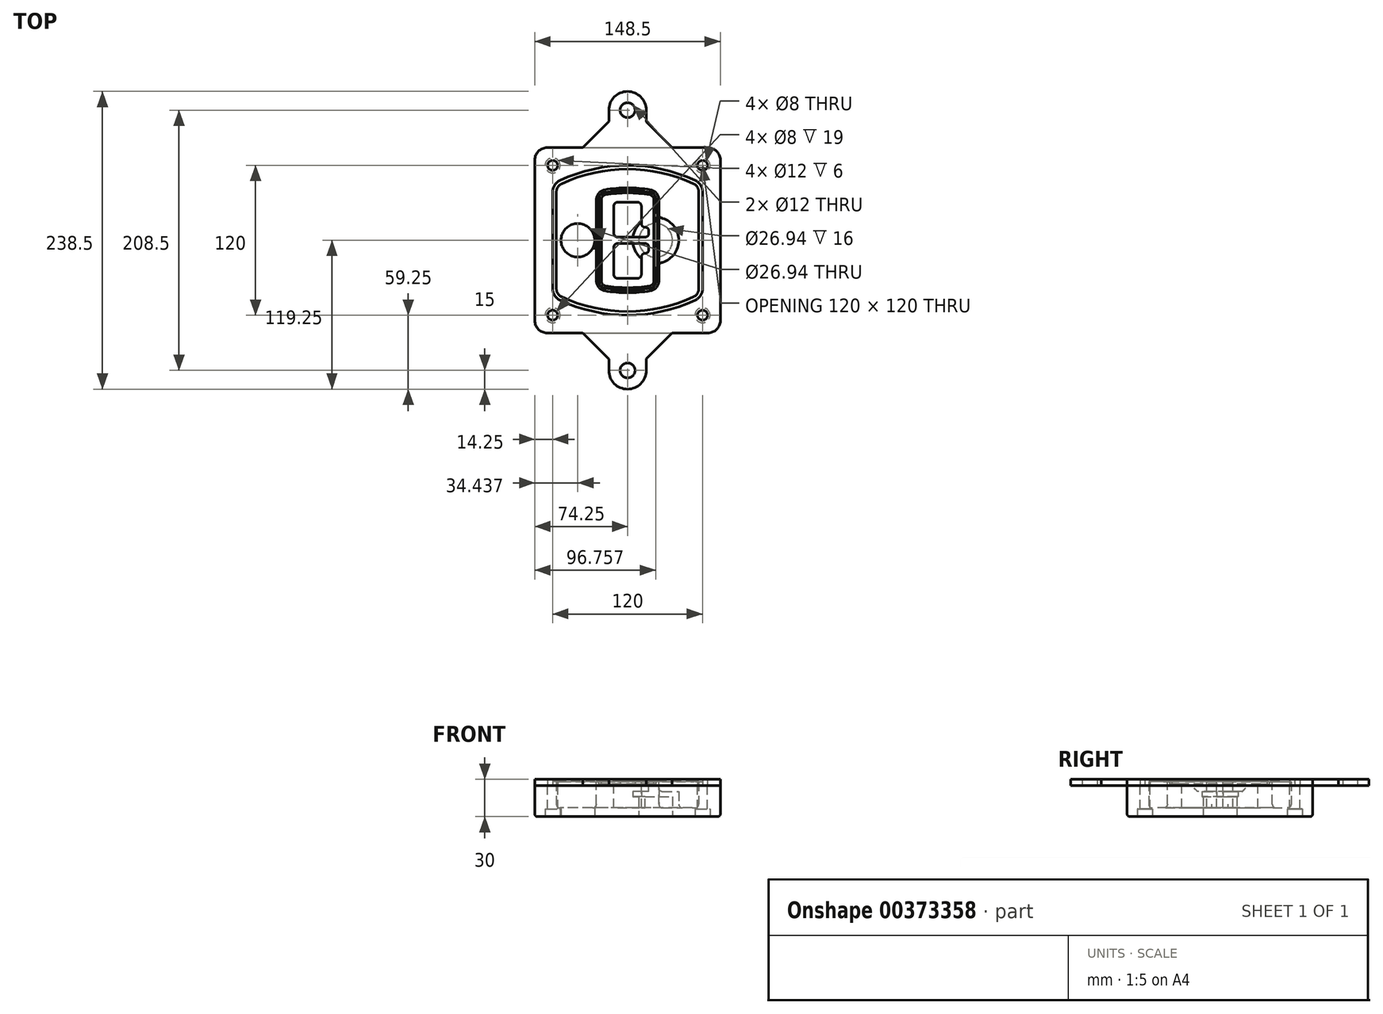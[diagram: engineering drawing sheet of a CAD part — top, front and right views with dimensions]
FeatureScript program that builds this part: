
annotation { "Feature Type Name" : "Feature", "Feature Type Description" : "" }
export const myFeature = defineFeature(function(context is Context, id is Id, definition is map)
    precondition{}
    {
        {
            var Q0;
            Q0=qCreatedBy(makeId("Top.planeOp"),FACE);
            var sketch = newSketch(context, id + "F0", { "sketchPlane" : qUnion([Q0])});
            skPoint(sketch, "E0.rect.middle", {"position": v(0, 0) * mm});
            skLineSegment(sketch, "E1.bottom", {"start": v(-64.25, -74.25) * mm, "end": v(64.25, -74.25) * mm});
            skLineSegment(sketch, "E1.top", {"start": v(-64.25, 74.25) * mm, "end": v(64.25, 74.25) * mm});
            skLineSegment(sketch, "E1.left", {"start": v(-74.25, -64.25) * mm, "end": v(-74.25, 64.25) * mm});
            skLineSegment(sketch, "E1.right", {"start": v(74.25, -64.25) * mm, "end": v(74.25, 64.25) * mm});
            skLineSegment(sketch, "E2", {"start": v(-74.25, 74.25) * mm, "end": v(74.25, -74.25) * mm, "construction": true});
            skLineSegment(sketch, "E3", {"start": v(74.25, 74.25) * mm, "end": v(-74.25, -74.25) * mm, "construction": true});
            skCircle(sketch, "E4", {"center": v(-60, 60) * mm, "radius": 4 * mm});
            skCircle(sketch, "E5", {"center": v(60, 60) * mm, "radius": 4 * mm});
            skCircle(sketch, "E6", {"center": v(60, -60) * mm, "radius": 4 * mm});
            skCircle(sketch, "E7", {"center": v(-60, -60) * mm, "radius": 4 * mm});
            skLineSegment(sketch, "E8", {"start": v(-60, 60) * mm, "end": v(60, 60) * mm, "construction": true});
            skLineSegment(sketch, "E9", {"start": v(60, 60) * mm, "end": v(60, -60) * mm, "construction": true});
            skLineSegment(sketch, "E10", {"start": v(60, -60) * mm, "end": v(-60, -60) * mm, "construction": true});
            skLineSegment(sketch, "E11", {"start": v(-60, -60) * mm, "end": v(-60, 60) * mm, "construction": true});
            skLineSegment(sketch, "E12", {"start": v(-60, 38.83) * mm, "end": v(-60, -38.83) * mm});
            skLineSegment(sketch, "E13", {"start": v(60, 38.83) * mm, "end": v(60, -38.83) * mm});
            skArc(sketch, "E14", {"start": v(54.26, 47.88) * mm, "mid": v(0, 60) * mm, "end": v(-54.26, 47.88) * mm});
            skArc(sketch, "E15", {"start": v(-54.26, -47.88) * mm, "mid": v(0, -60) * mm, "end": v(54.26, -47.88) * mm});
            skLineSegment(sketch, "E16", {"start": v(-60, 0) * mm, "end": v(60, 0) * mm, "construction": true});
            skPoint(sketch, "E17.visualSharp", {"position": v(-60, -45) * mm});
            skArc(sketch, "E17.filletArc", {"start": v(-60, -38.83) * mm, "mid": v(-58.44, -44.2) * mm, "end": v(-54.26, -47.88) * mm});
            skPoint(sketch, "E18.visualSharp", {"position": v(-60, 45) * mm});
            skArc(sketch, "E18.filletArc", {"start": v(-54.26, 47.88) * mm, "mid": v(-58.44, 44.2) * mm, "end": v(-60, 38.83) * mm});
            skPoint(sketch, "E19.visualSharp", {"position": v(60, 45) * mm});
            skArc(sketch, "E19.filletArc", {"start": v(60, 38.83) * mm, "mid": v(58.44, 44.2) * mm, "end": v(54.26, 47.88) * mm});
            skPoint(sketch, "E20.visualSharp", {"position": v(60, -45) * mm});
            skArc(sketch, "E20.filletArc", {"start": v(54.26, -47.88) * mm, "mid": v(58.44, -44.2) * mm, "end": v(60, -38.83) * mm});
            skPoint(sketch, "E21.visualSharp", {"position": v(-74.25, 74.25) * mm});
            skArc(sketch, "E21.filletArc", {"start": v(-64.25, 74.25) * mm, "mid": v(-71.32, 71.32) * mm, "end": v(-74.25, 64.25) * mm});
            skPoint(sketch, "E22.visualSharp", {"position": v(74.25, 74.25) * mm});
            skArc(sketch, "E22.filletArc", {"start": v(74.25, 64.25) * mm, "mid": v(71.32, 71.32) * mm, "end": v(64.25, 74.25) * mm});
            skPoint(sketch, "E23.visualSharp", {"position": v(74.25, -74.25) * mm});
            skArc(sketch, "E23.filletArc", {"start": v(64.25, -74.25) * mm, "mid": v(71.32, -71.32) * mm, "end": v(74.25, -64.25) * mm});
            skPoint(sketch, "E24.visualSharp", {"position": v(-74.25, -74.25) * mm});
            skArc(sketch, "E24.filletArc", {"start": v(-74.25, -64.25) * mm, "mid": v(-71.32, -71.32) * mm, "end": v(-64.25, -74.25) * mm});
            skArc(sketch, "E25.0", {"start": v(57, 38.83) * mm, "mid": v(55.9, 42.58) * mm, "end": v(52.98, 45.17) * mm});
            skLineSegment(sketch, "E25.1", {"start": v(57, 38.83) * mm, "end": v(57, -38.83) * mm});
            skArc(sketch, "E25.2", {"start": v(52.98, -45.17) * mm, "mid": v(55.9, -42.58) * mm, "end": v(57, -38.83) * mm});
            skArc(sketch, "E25.3", {"start": v(-52.98, -45.17) * mm, "mid": v(0, -57) * mm, "end": v(52.98, -45.17) * mm});
            skArc(sketch, "E25.4", {"start": v(-57, -38.83) * mm, "mid": v(-55.9, -42.58) * mm, "end": v(-52.98, -45.17) * mm});
            skArc(sketch, "E25.5", {"start": v(52.98, 45.17) * mm, "mid": v(0, 57) * mm, "end": v(-52.98, 45.17) * mm});
            skLineSegment(sketch, "E25.6", {"start": v(-57, 38.83) * mm, "end": v(-57, -38.83) * mm});
            skArc(sketch, "E25.7", {"start": v(-52.98, 45.17) * mm, "mid": v(-55.9, 42.58) * mm, "end": v(-57, 38.83) * mm});
            skArc(sketch, "E26.0", {"start": v(-55.96, 51.5) * mm, "mid": v(-61.82, 46.33) * mm, "end": v(-64, 38.83) * mm});
            skArc(sketch, "E26.1", {"start": v(55.96, 51.5) * mm, "mid": v(0, 64) * mm, "end": v(-55.96, 51.5) * mm});
            skArc(sketch, "E26.2", {"start": v(64, 38.83) * mm, "mid": v(61.82, 46.33) * mm, "end": v(55.96, 51.5) * mm});
            skLineSegment(sketch, "E26.3", {"start": v(64, 38.83) * mm, "end": v(64, -38.83) * mm});
            skArc(sketch, "E26.4", {"start": v(55.96, -51.5) * mm, "mid": v(61.82, -46.33) * mm, "end": v(64, -38.83) * mm});
            skLineSegment(sketch, "E26.5", {"start": v(-64, 38.83) * mm, "end": v(-64, -38.83) * mm});
            skArc(sketch, "E26.6", {"start": v(-55.96, -51.5) * mm, "mid": v(0, -64) * mm, "end": v(55.96, -51.5) * mm});
            skArc(sketch, "E26.7", {"start": v(-64, -38.83) * mm, "mid": v(-61.82, -46.33) * mm, "end": v(-55.96, -51.5) * mm});
            skSolve(sketch);
        }
        {
            var Q0;
            Q0=makeQuery(id+"F0.imprint","IMPRINT",FACE,{"disambiguationData":[TD([[makeQuery(id+"F0.imprint","IMPRINT",EDGE,{"derivedFrom":sQuery(id+"F0.wireOp",EDGE,"E1.bottom")}),1.0]])]});
            var Q1;
            Q1=makeQuery(id+"F0.imprint","IMPRINT",FACE,{"disambiguationData":[TD([[makeQuery(id+"F0.imprint","IMPRINT",EDGE,{"derivedFrom":sQuery(id+"F0.wireOp",EDGE,"E12")}),1.0]])]});
            var Q2;
            Q2=makeQuery(id+"F0.imprint","IMPRINT",FACE,{"disambiguationData":[TD([[makeQuery(id+"F0.imprint","IMPRINT",EDGE,{"derivedFrom":sQuery(id+"F0.wireOp",EDGE,"E25.0")}),1.0]])]});
            var Q3;
            Q3=makeQuery(id+"F0.imprint","IMPRINT",FACE,{"disambiguationData":[TD([[makeQuery(id+"F0.imprint","IMPRINT",EDGE,{"derivedFrom":sQuery(id+"F0.wireOp",EDGE,"E12")}),-1.0]])]});
            extrude(context, id + "F1", {"entities" : qUnion([Q0, Q1, Q2, Q3]), "oppositeDirection" : true, "depth" : 25 * mm});
        }
        {
            var Q0;
            Q0=makeQuery(id+"F0.imprint","IMPRINT",FACE,{"disambiguationData":[TD([[makeQuery(id+"F0.imprint","IMPRINT",EDGE,{"derivedFrom":sQuery(id+"F0.wireOp",EDGE,"E12")}),1.0]])]});
            extrude(context, id + "F2", {"entities" : qUnion([Q0]), "operationType" : NewBodyOperationType.ADD, "depth" : 3 * mm});
        }
        {
            var Q0;
            Q0=makeQuery(id+"F0.imprint","IMPRINT",FACE,{"disambiguationData":[TD([[makeQuery(id+"F0.imprint","IMPRINT",EDGE,{"derivedFrom":sQuery(id+"F0.wireOp",EDGE,"E25.0")}),1.0]])]});
            extrude(context, id + "F3", {"entities" : qUnion([Q0]), "operationType" : NewBodyOperationType.REMOVE, "oppositeDirection" : true, "depth" : 18 * mm});
        }
        {
            var Q0;
            Q0=makeQuery(id+"F2.opExtrude","CAP_FACE",FACE,{"disambiguationData":[OSD([sQuery(id+"F0.wireOp",EDGE,"E12"),sQuery(id+"F0.wireOp",EDGE,"E13"),sQuery(id+"F0.wireOp",EDGE,"E14"),sQuery(id+"F0.wireOp",EDGE,"E15"),sQuery(id+"F0.wireOp",EDGE,"E17.filletArc"),sQuery(id+"F0.wireOp",EDGE,"E18.filletArc"),sQuery(id+"F0.wireOp",EDGE,"E19.filletArc"),sQuery(id+"F0.wireOp",EDGE,"E20.filletArc"),sQuery(id+"F0.wireOp",EDGE,"E25.0"),sQuery(id+"F0.wireOp",EDGE,"E25.1"),sQuery(id+"F0.wireOp",EDGE,"E25.2"),sQuery(id+"F0.wireOp",EDGE,"E25.3"),sQuery(id+"F0.wireOp",EDGE,"E25.4"),sQuery(id+"F0.wireOp",EDGE,"E25.5"),sQuery(id+"F0.wireOp",EDGE,"E25.6"),sQuery(id+"F0.wireOp",EDGE,"E25.7")])],"isStart":false});
            var sketch = newSketch(context, id + "F4", { "sketchPlane" : qUnion([Q0])});
            skArc(sketch, "E27.0", {"start": v(-18.34, -40.45) * mm, "mid": v(0, -42) * mm, "end": v(18.34, -40.45) * mm});
            skArc(sketch, "E28.0", {"start": v(18.34, 40.45) * mm, "mid": v(0, 42) * mm, "end": v(-18.34, 40.45) * mm});
            skLineSegment(sketch, "E29", {"start": v(-25, 32.57) * mm, "end": v(-25, -32.57) * mm});
            skLineSegment(sketch, "E30", {"start": v(25, 32.57) * mm, "end": v(25, -32.57) * mm});
            skLineSegment(sketch, "E31", {"start": v(-25, 39.1) * mm, "end": v(25, 39.1) * mm, "construction": true});
            skLineSegment(sketch, "E32", {"start": v(-25, -39.1) * mm, "end": v(25, -39.1) * mm, "construction": true});
            skPoint(sketch, "E33.visualSharp", {"position": v(-25, 39.1) * mm});
            skArc(sketch, "E33.filletArc", {"start": v(-18.34, 40.45) * mm, "mid": v(-23.11, 37.73) * mm, "end": v(-25, 32.57) * mm});
            skPoint(sketch, "E34.visualSharp", {"position": v(25, 39.1) * mm});
            skArc(sketch, "E34.filletArc", {"start": v(25, 32.57) * mm, "mid": v(23.11, 37.73) * mm, "end": v(18.34, 40.45) * mm});
            skPoint(sketch, "E35.visualSharp", {"position": v(25, -39.1) * mm});
            skArc(sketch, "E35.filletArc", {"start": v(18.34, -40.45) * mm, "mid": v(23.11, -37.73) * mm, "end": v(25, -32.57) * mm});
            skPoint(sketch, "E36.visualSharp", {"position": v(-25, -39.1) * mm});
            skArc(sketch, "E36.filletArc", {"start": v(-25, -32.57) * mm, "mid": v(-23.11, -37.73) * mm, "end": v(-18.34, -40.45) * mm});
            skArc(sketch, "E37.0", {"start": v(52.98, 45.17) * mm, "mid": v(0, 57) * mm, "end": v(-52.98, 45.17) * mm});
            skArc(sketch, "E37.1", {"start": v(-52.98, 45.17) * mm, "mid": v(-55.9, 42.58) * mm, "end": v(-57, 38.83) * mm});
            skLineSegment(sketch, "E37.2", {"start": v(-57, 38.83) * mm, "end": v(-57, -38.83) * mm});
            skArc(sketch, "E37.3", {"start": v(-57, -38.83) * mm, "mid": v(-55.9, -42.58) * mm, "end": v(-52.98, -45.17) * mm});
            skArc(sketch, "E37.4", {"start": v(-52.98, -45.17) * mm, "mid": v(0, -57) * mm, "end": v(52.98, -45.17) * mm});
            skArc(sketch, "E37.5", {"start": v(52.98, -45.17) * mm, "mid": v(55.9, -42.58) * mm, "end": v(57, -38.83) * mm});
            skLineSegment(sketch, "E37.6", {"start": v(57, 38.83) * mm, "end": v(57, -38.83) * mm});
            skArc(sketch, "E37.7", {"start": v(57, 38.83) * mm, "mid": v(55.9, 42.58) * mm, "end": v(52.98, 45.17) * mm});
            skLineSegment(sketch, "E38.0", {"start": v(23, 32.57) * mm, "end": v(23, -32.57) * mm});
            skArc(sketch, "E38.1", {"start": v(18, -38.48) * mm, "mid": v(21.58, -36.44) * mm, "end": v(23, -32.57) * mm});
            skArc(sketch, "E38.2", {"start": v(-18, -38.48) * mm, "mid": v(0, -40) * mm, "end": v(18, -38.48) * mm});
            skArc(sketch, "E38.3", {"start": v(-23, -32.57) * mm, "mid": v(-21.58, -36.44) * mm, "end": v(-18, -38.48) * mm});
            skLineSegment(sketch, "E38.4", {"start": v(-23, 32.57) * mm, "end": v(-23, -32.57) * mm});
            skArc(sketch, "E38.5", {"start": v(23, 32.57) * mm, "mid": v(21.58, 36.44) * mm, "end": v(18, 38.48) * mm});
            skArc(sketch, "E38.6", {"start": v(-18, 38.48) * mm, "mid": v(-21.58, 36.44) * mm, "end": v(-23, 32.57) * mm});
            skArc(sketch, "E38.7", {"start": v(18, 38.48) * mm, "mid": v(0, 40) * mm, "end": v(-18, 38.48) * mm});
            skArc(sketch, "E39.0", {"start": v(21, 32.57) * mm, "mid": v(20.06, 35.15) * mm, "end": v(17.67, 36.5) * mm});
            skLineSegment(sketch, "E39.1", {"start": v(21, 32.57) * mm, "end": v(21, -32.57) * mm});
            skArc(sketch, "E39.2", {"start": v(17.67, -36.5) * mm, "mid": v(20.06, -35.15) * mm, "end": v(21, -32.57) * mm});
            skArc(sketch, "E39.3", {"start": v(-17.67, -36.5) * mm, "mid": v(0, -38) * mm, "end": v(17.67, -36.5) * mm});
            skArc(sketch, "E39.4", {"start": v(-21, -32.57) * mm, "mid": v(-20.06, -35.15) * mm, "end": v(-17.67, -36.5) * mm});
            skArc(sketch, "E39.5", {"start": v(17.67, 36.5) * mm, "mid": v(0, 38) * mm, "end": v(-17.67, 36.5) * mm});
            skLineSegment(sketch, "E39.6", {"start": v(-21, 32.57) * mm, "end": v(-21, -32.57) * mm});
            skArc(sketch, "E39.7", {"start": v(-17.67, 36.5) * mm, "mid": v(-20.06, 35.15) * mm, "end": v(-21, 32.57) * mm});
            skLineSegment(sketch, "E40", {"start": v(-25, 0) * mm, "end": v(25, 0) * mm, "construction": true});
            skLineSegment(sketch, "E41", {"start": v(-11, 5.5) * mm, "end": v(-11, 27.5) * mm});
            skLineSegment(sketch, "E42", {"start": v(-8, 30.5) * mm, "end": v(8, 30.5) * mm});
            skLineSegment(sketch, "E43", {"start": v(11, 27.5) * mm, "end": v(11, 13.5) * mm});
            skLineSegment(sketch, "E44", {"start": v(14, 10.5) * mm, "end": v(14, 10.5) * mm});
            skLineSegment(sketch, "E45", {"start": v(17, 7.5) * mm, "end": v(17, 5.5) * mm});
            skLineSegment(sketch, "E46", {"start": v(14, 2.5) * mm, "end": v(-8, 2.5) * mm});
            skPoint(sketch, "E47.visualSharp", {"position": v(-11, 30.5) * mm});
            skArc(sketch, "E47.filletArc", {"start": v(-8, 30.5) * mm, "mid": v(-10.12, 29.62) * mm, "end": v(-11, 27.5) * mm});
            skPoint(sketch, "E48.visualSharp", {"position": v(11, 30.5) * mm});
            skArc(sketch, "E48.filletArc", {"start": v(11, 27.5) * mm, "mid": v(10.12, 29.62) * mm, "end": v(8, 30.5) * mm});
            skPoint(sketch, "E49.visualSharp", {"position": v(11, 10.5) * mm});
            skArc(sketch, "E49.filletArc", {"start": v(11, 13.5) * mm, "mid": v(11.88, 11.38) * mm, "end": v(14, 10.5) * mm});
            skPoint(sketch, "E50.visualSharp", {"position": v(17, 10.5) * mm});
            skArc(sketch, "E50.filletArc", {"start": v(17, 7.5) * mm, "mid": v(16.12, 9.62) * mm, "end": v(14, 10.5) * mm});
            skPoint(sketch, "E51.visualSharp", {"position": v(17, 2.5) * mm});
            skArc(sketch, "E51.filletArc", {"start": v(14, 2.5) * mm, "mid": v(16.12, 3.38) * mm, "end": v(17, 5.5) * mm});
            skPoint(sketch, "E52.visualSharp", {"position": v(-11, 2.5) * mm});
            skArc(sketch, "E52.filletArc", {"start": v(-11, 5.5) * mm, "mid": v(-10.12, 3.38) * mm, "end": v(-8, 2.5) * mm});
            skLineSegment(sketch, "E53.0.MirrorCS", {"start": v(14, -2.5) * mm, "end": v(-8, -2.5) * mm});
            skArc(sketch, "E54.0.MirrorCS", {"start": v(-11, -5.5) * mm, "mid": v(-10.12, -3.38) * mm, "end": v(-8, -2.5) * mm});
            skLineSegment(sketch, "E55.0.MirrorCS", {"start": v(-11, -5.5) * mm, "end": v(-11, -27.5) * mm});
            skArc(sketch, "E56.0.MirrorCS", {"start": v(-8, -30.5) * mm, "mid": v(-10.12, -29.62) * mm, "end": v(-11, -27.5) * mm});
            skLineSegment(sketch, "E57.0.MirrorCS", {"start": v(-8, -30.5) * mm, "end": v(8, -30.5) * mm});
            skArc(sketch, "E58.0.MirrorCS", {"start": v(11, -27.5) * mm, "mid": v(10.12, -29.62) * mm, "end": v(8, -30.5) * mm});
            skLineSegment(sketch, "E59.0.MirrorCS", {"start": v(11, -27.5) * mm, "end": v(11, -13.5) * mm});
            skArc(sketch, "E60.0.MirrorCS", {"start": v(11, -13.5) * mm, "mid": v(11.88, -11.38) * mm, "end": v(14, -10.5) * mm});
            skArc(sketch, "E61.0.MirrorCS", {"start": v(17, -7.5) * mm, "mid": v(16.12, -9.62) * mm, "end": v(14, -10.5) * mm});
            skLineSegment(sketch, "E62.0.MirrorCS", {"start": v(17, -7.5) * mm, "end": v(17, -5.5) * mm});
            skArc(sketch, "E63.0.MirrorCS", {"start": v(14, -2.5) * mm, "mid": v(16.12, -3.38) * mm, "end": v(17, -5.5) * mm});
            skSolve(sketch);
        }
        {
            var Q0;
            Q0=makeQuery(id+"F4.imprint","IMPRINT",FACE,{"disambiguationData":[TD([[makeQuery(id+"F4.imprint","IMPRINT",EDGE,{"derivedFrom":sQuery(id+"F4.wireOp",EDGE,"E27.0")}),1.0]])]});
            var Q1;
            Q1=makeQuery(id+"F4.imprint","IMPRINT",FACE,{"disambiguationData":[TD([[makeQuery(id+"F4.imprint","IMPRINT",EDGE,{"derivedFrom":sQuery(id+"F4.wireOp",EDGE,"E38.0")}),-1.0]])]});
            var Q2;
            Q2=makeQuery(id+"F4.imprint","IMPRINT",FACE,{"disambiguationData":[TD([[makeQuery(id+"F4.imprint","IMPRINT",EDGE,{"derivedFrom":sQuery(id+"F4.wireOp",EDGE,"E39.0")}),1.0]])]});
            extrude(context, id + "F5", {"entities" : qUnion([Q0, Q1, Q2]), "operationType" : NewBodyOperationType.ADD, "endBound" : BoundingType.UP_TO_NEXT, "oppositeDirection" : true, "depth" : 25 * mm});
        }
        {
            var Q0;
            Q0=makeQuery(id+"F4.imprint","IMPRINT",FACE,{"disambiguationData":[TD([[makeQuery(id+"F4.imprint","IMPRINT",EDGE,{"derivedFrom":sQuery(id+"F4.wireOp",EDGE,"E38.0")}),-1.0]])]});
            extrude(context, id + "F6", {"entities" : qUnion([Q0]), "operationType" : NewBodyOperationType.REMOVE, "oppositeDirection" : true, "depth" : 2 * mm});
        }
        {
            var Q0;
            Q0=makeQuery(id+"F1.opExtrude","CAP_FACE",FACE,{"disambiguationData":[OSD([sQuery(id+"F0.wireOp",EDGE,"E1.bottom"),sQuery(id+"F0.wireOp",EDGE,"E1.top"),sQuery(id+"F0.wireOp",EDGE,"E1.left"),sQuery(id+"F0.wireOp",EDGE,"E1.right"),sQuery(id+"F0.wireOp",EDGE,"E4"),sQuery(id+"F0.wireOp",EDGE,"E5"),sQuery(id+"F0.wireOp",EDGE,"E6"),sQuery(id+"F0.wireOp",EDGE,"E7"),sQuery(id+"F0.wireOp",EDGE,"E21.filletArc"),sQuery(id+"F0.wireOp",EDGE,"E22.filletArc"),sQuery(id+"F0.wireOp",EDGE,"E23.filletArc"),sQuery(id+"F0.wireOp",EDGE,"E24.filletArc")])],"isStart":false});
            var sketch = newSketch(context, id + "F7", { "sketchPlane" : qUnion([Q0])});
            skCircle(sketch, "E64", {"center": v(22.5, 0) * mm, "radius": 13.47 * mm});
            skCircle(sketch, "E65", {"center": v(-39.81, 0) * mm, "radius": 13.47 * mm});
            skLineSegment(sketch, "E66", {"start": v(74.25, 0) * mm, "end": v(-74.25, 0) * mm});
            skCircle(sketch, "E67", {"center": v(22.5, 0) * mm, "radius": 18.47 * mm});
            skCircle(sketch, "E68", {"center": v(60, -60) * mm, "radius": 6 * mm});
            skCircle(sketch, "E69", {"center": v(-60, -60) * mm, "radius": 6 * mm});
            skCircle(sketch, "E70", {"center": v(-60, 60) * mm, "radius": 6 * mm});
            skCircle(sketch, "E71", {"center": v(60, 60) * mm, "radius": 6 * mm});
            skSolve(sketch);
        }
        {
            var Q0;
            {var subQ1=sQuery(id+"F7.wireOp",EDGE,"E66");var subQ4=sQuery(id+"F7.wireOp",EDGE,"E64");var subQ6=makeQuery(id+"F7.imprint","INTERSECT",VERTEX,{"disambiguationData":[OD(0.0)],"derivedFrom":[subQ4,subQ1]});Q0=makeQuery(id+"F7.imprint","IMPRINT",FACE,{"disambiguationData":[TD([[makeQuery(id+"F7.imprint","IMPRINT",EDGE,{"disambiguationData":[TD([[subQ6,-1.0]])],"derivedFrom":subQ4}),-1.0]])]});}
            var Q1;
            {var subQ0=sQuery(id+"F7.wireOp",EDGE,"E66");var subQ1=sQuery(id+"F7.wireOp",EDGE,"E64");var subQ3=makeQuery(id+"F7.imprint","INTERSECT",VERTEX,{"disambiguationData":[OD(0.0)],"derivedFrom":[subQ1,subQ0]});Q1=makeQuery(id+"F7.imprint","IMPRINT",FACE,{"disambiguationData":[TD([[makeQuery(id+"F7.imprint","IMPRINT",EDGE,{"disambiguationData":[TD([[subQ3,-1.0]])],"derivedFrom":subQ1}),1.0]])]});}
            var Q2;
            {var subQ0=sQuery(id+"F7.wireOp",EDGE,"E66");var subQ1=sQuery(id+"F7.wireOp",EDGE,"E64");var subQ3=makeQuery(id+"F7.imprint","INTERSECT",VERTEX,{"disambiguationData":[OD(0.0)],"derivedFrom":[subQ1,subQ0]});Q2=makeQuery(id+"F7.imprint","IMPRINT",FACE,{"disambiguationData":[TD([[makeQuery(id+"F7.imprint","IMPRINT",EDGE,{"disambiguationData":[TD([[subQ3,1.0]])],"derivedFrom":subQ1}),1.0]])]});}
            var Q3;
            {var subQ1=sQuery(id+"F7.wireOp",EDGE,"E66");var subQ4=sQuery(id+"F7.wireOp",EDGE,"E64");var subQ6=makeQuery(id+"F7.imprint","INTERSECT",VERTEX,{"disambiguationData":[OD(0.0)],"derivedFrom":[subQ4,subQ1]});Q3=makeQuery(id+"F7.imprint","IMPRINT",FACE,{"disambiguationData":[TD([[makeQuery(id+"F7.imprint","IMPRINT",EDGE,{"disambiguationData":[TD([[subQ6,1.0]])],"derivedFrom":subQ4}),-1.0]])]});}
            extrude(context, id + "F8", {"entities" : qUnion([Q0, Q1, Q2, Q3]), "operationType" : NewBodyOperationType.ADD, "oppositeDirection" : true, "depth" : 20 * mm});
        }
        {
            var Q0;
            {var subQ0=sQuery(id+"F7.wireOp",EDGE,"E66");var subQ1=sQuery(id+"F7.wireOp",EDGE,"E64");var subQ3=makeQuery(id+"F7.imprint","INTERSECT",VERTEX,{"disambiguationData":[OD(0.0)],"derivedFrom":[subQ1,subQ0]});Q0=makeQuery(id+"F7.imprint","IMPRINT",FACE,{"disambiguationData":[TD([[makeQuery(id+"F7.imprint","IMPRINT",EDGE,{"disambiguationData":[TD([[subQ3,-1.0]])],"derivedFrom":subQ1}),1.0]])]});}
            var Q1;
            {var subQ0=sQuery(id+"F7.wireOp",EDGE,"E66");var subQ1=sQuery(id+"F7.wireOp",EDGE,"E64");var subQ3=makeQuery(id+"F7.imprint","INTERSECT",VERTEX,{"disambiguationData":[OD(0.0)],"derivedFrom":[subQ1,subQ0]});Q1=makeQuery(id+"F7.imprint","IMPRINT",FACE,{"disambiguationData":[TD([[makeQuery(id+"F7.imprint","IMPRINT",EDGE,{"disambiguationData":[TD([[subQ3,1.0]])],"derivedFrom":subQ1}),1.0]])]});}
            extrude(context, id + "F9", {"entities" : qUnion([Q0, Q1]), "operationType" : NewBodyOperationType.REMOVE, "oppositeDirection" : true, "depth" : 16 * mm});
        }
        {
            var Q0;
            {var subQ0=sQuery(id+"F7.wireOp",EDGE,"E66");var subQ1=sQuery(id+"F7.wireOp",EDGE,"E65");var subQ3=makeQuery(id+"F7.imprint","INTERSECT",VERTEX,{"disambiguationData":[OD(0.0)],"derivedFrom":[subQ1,subQ0]});Q0=makeQuery(id+"F7.imprint","IMPRINT",FACE,{"disambiguationData":[TD([[makeQuery(id+"F7.imprint","IMPRINT",EDGE,{"disambiguationData":[TD([[subQ3,-1.0]])],"derivedFrom":subQ1}),1.0]])]});}
            var Q1;
            {var subQ0=sQuery(id+"F7.wireOp",EDGE,"E66");var subQ1=sQuery(id+"F7.wireOp",EDGE,"E65");var subQ3=makeQuery(id+"F7.imprint","INTERSECT",VERTEX,{"disambiguationData":[OD(0.0)],"derivedFrom":[subQ1,subQ0]});Q1=makeQuery(id+"F7.imprint","IMPRINT",FACE,{"disambiguationData":[TD([[makeQuery(id+"F7.imprint","IMPRINT",EDGE,{"disambiguationData":[TD([[subQ3,1.0]])],"derivedFrom":subQ1}),1.0]])]});}
            extrude(context, id + "F10", {"entities" : qUnion([Q0, Q1]), "operationType" : NewBodyOperationType.REMOVE, "oppositeDirection" : true, "depth" : 25 * mm});
        }
        {
            var Q0;
            Q0=makeQuery(id+"F7.imprint","IMPRINT",FACE,{"disambiguationData":[TD([[makeQuery(id+"F7.imprint","IMPRINT",EDGE,{"derivedFrom":sQuery(id+"F7.wireOp",EDGE,"E68")}),1.0]])]});
            var Q1;
            Q1=makeQuery(id+"F7.imprint","IMPRINT",FACE,{"disambiguationData":[TD([[makeQuery(id+"F7.imprint","IMPRINT",EDGE,{"derivedFrom":makeQuery(id+"F1.opExtrude","CAP_EDGE",EDGE,{"disambiguationData":[OSD([sQuery(id+"F0.wireOp",EDGE,"E5")])],"isStart":false})}),-1.0]])]});
            var Q2;
            Q2=makeQuery(id+"F7.imprint","IMPRINT",FACE,{"disambiguationData":[TD([[makeQuery(id+"F7.imprint","IMPRINT",EDGE,{"derivedFrom":sQuery(id+"F7.wireOp",EDGE,"E69")}),1.0]])]});
            var Q3;
            Q3=makeQuery(id+"F7.imprint","IMPRINT",FACE,{"disambiguationData":[TD([[makeQuery(id+"F7.imprint","IMPRINT",EDGE,{"derivedFrom":makeQuery(id+"F1.opExtrude","CAP_EDGE",EDGE,{"disambiguationData":[OSD([sQuery(id+"F0.wireOp",EDGE,"E4")])],"isStart":false})}),-1.0]])]});
            var Q4;
            Q4=makeQuery(id+"F7.imprint","IMPRINT",FACE,{"disambiguationData":[TD([[makeQuery(id+"F7.imprint","IMPRINT",EDGE,{"derivedFrom":sQuery(id+"F7.wireOp",EDGE,"E70")}),1.0]])]});
            var Q5;
            Q5=makeQuery(id+"F7.imprint","IMPRINT",FACE,{"disambiguationData":[TD([[makeQuery(id+"F7.imprint","IMPRINT",EDGE,{"derivedFrom":makeQuery(id+"F1.opExtrude","CAP_EDGE",EDGE,{"disambiguationData":[OSD([sQuery(id+"F0.wireOp",EDGE,"E7")])],"isStart":false})}),-1.0]])]});
            var Q6;
            Q6=makeQuery(id+"F7.imprint","IMPRINT",FACE,{"disambiguationData":[TD([[makeQuery(id+"F7.imprint","IMPRINT",EDGE,{"derivedFrom":sQuery(id+"F7.wireOp",EDGE,"E71")}),1.0]])]});
            var Q7;
            Q7=makeQuery(id+"F7.imprint","IMPRINT",FACE,{"disambiguationData":[TD([[makeQuery(id+"F7.imprint","IMPRINT",EDGE,{"derivedFrom":makeQuery(id+"F1.opExtrude","CAP_EDGE",EDGE,{"disambiguationData":[OSD([sQuery(id+"F0.wireOp",EDGE,"E6")])],"isStart":false})}),-1.0]])]});
            extrude(context, id + "F11", {"entities" : qUnion([Q0, Q1, Q2, Q3, Q4, Q5, Q6, Q7]), "operationType" : NewBodyOperationType.REMOVE, "oppositeDirection" : true, "depth" : 6 * mm});
        }
        {
            var Q0;
            Q0=makeQuery(id+"F9.boolean.opBoolean","COPY",FACE,{"derivedFrom":makeQuery(id+"F9.opExtrude","CAP_FACE",FACE,{"disambiguationData":[OSD([sQuery(id+"F7.wireOp",EDGE,"E64")])],"isStart":false})});
            var sketch = newSketch(context, id + "F12", { "sketchPlane" : qUnion([Q0])});
            skArc(sketch, "E72.0", {"start": v(11, 14.45) * mm, "mid": v(6.45, 9.13) * mm, "end": v(4.2, 2.5) * mm});
            skArc(sketch, "E72.1", {"start": v(4.2, -2.5) * mm, "mid": v(6.45, -9.13) * mm, "end": v(11, -14.45) * mm});
            skLineSegment(sketch, "E73", {"start": v(4.2, -2.5) * mm, "end": v(14, -2.5) * mm});
            skLineSegment(sketch, "E74.0", {"start": v(14, 2.5) * mm, "end": v(4.2, 2.5) * mm});
            skArc(sketch, "E74.1", {"start": v(14, 2.5) * mm, "mid": v(16.12, 3.38) * mm, "end": v(17, 5.5) * mm});
            skLineSegment(sketch, "E74.2", {"start": v(17, 7.5) * mm, "end": v(17, 5.5) * mm});
            skArc(sketch, "E74.3", {"start": v(17, 7.5) * mm, "mid": v(16.12, 9.62) * mm, "end": v(14, 10.5) * mm});
            skArc(sketch, "E74.4", {"start": v(11, 13.5) * mm, "mid": v(11.88, 11.38) * mm, "end": v(14, 10.5) * mm});
            skLineSegment(sketch, "E74.5", {"start": v(11, 14.45) * mm, "end": v(11, 13.5) * mm});
            skLineSegment(sketch, "E74.7", {"start": v(14, -2.5) * mm, "end": v(4.2, -2.5) * mm});
            skArc(sketch, "E74.8", {"start": v(14, -2.5) * mm, "mid": v(16.12, -3.38) * mm, "end": v(17, -5.5) * mm});
            skLineSegment(sketch, "E74.9", {"start": v(17, -7.5) * mm, "end": v(17, -5.5) * mm});
            skArc(sketch, "E74.10", {"start": v(17, -7.5) * mm, "mid": v(16.12, -9.62) * mm, "end": v(14, -10.5) * mm});
            skArc(sketch, "E74.11", {"start": v(11, -13.5) * mm, "mid": v(11.88, -11.38) * mm, "end": v(14, -10.5) * mm});
            skLineSegment(sketch, "E74.12", {"start": v(11, -14.45) * mm, "end": v(11, -13.5) * mm});
            skPoint(sketch, "E75.orphan", {"position": v(11, -27.5) * mm});
            skPoint(sketch, "E76.orphan", {"position": v(-8, -2.5) * mm});
            skPoint(sketch, "E77.orphan", {"position": v(-8, 2.5) * mm});
            skPoint(sketch, "E78.orphan", {"position": v(11, 27.5) * mm});
            skSolve(sketch);
        }
        {
            var Q0;
            {var subQ7=sQuery(id+"F12.wireOp",EDGE,"E72.0");var subQ14=sQuery(id+"F12.wireOp",EDGE,"E72.1");var subQ16=sQuery(id+"F12.wireOp",EDGE,"E74.1");var subQ18=sQuery(id+"F12.wireOp",EDGE,"E74.8");Q0=qUnion([makeQuery(id+"F12.imprint","IMPRINT",FACE,{"disambiguationData":[TD([[makeQuery(id+"F12.imprint","IMPRINT",EDGE,{"derivedFrom":subQ7}),1.0]])]}),makeQuery(id+"F12.imprint","IMPRINT",FACE,{"disambiguationData":[TD([[makeQuery(id+"F12.imprint","IMPRINT",EDGE,{"derivedFrom":subQ14}),1.0]])]}),makeQuery(id+"F12.imprint","IMPRINT",FACE,{"disambiguationData":[TD([[makeQuery(id+"F12.imprint","IMPRINT",EDGE,{"derivedFrom":subQ16}),1.0]])]}),makeQuery(id+"F12.imprint","IMPRINT",FACE,{"disambiguationData":[TD([[makeQuery(id+"F12.imprint","IMPRINT",EDGE,{"derivedFrom":subQ18}),-1.0]])]})]);}
            var Q1;
            Q1=makeQuery(id+"F5.boolean.opBoolean","SPLIT",FACE,{"disambiguationData":[TD([makeQuery(id+"F5.opExtrude","SWEPT_FACE",FACE,{"disambiguationData":[OSD([sQuery(id+"F4.wireOp",EDGE,"E41")])]})])],"derivedFrom":makeQuery(id+"F3.boolean.opBoolean","COPY",FACE,{"derivedFrom":makeQuery(id+"F3.opExtrude","CAP_FACE",FACE,{"disambiguationData":[OSD([sQuery(id+"F0.wireOp",EDGE,"E25.0"),sQuery(id+"F0.wireOp",EDGE,"E25.1"),sQuery(id+"F0.wireOp",EDGE,"E25.2"),sQuery(id+"F0.wireOp",EDGE,"E25.3"),sQuery(id+"F0.wireOp",EDGE,"E25.4"),sQuery(id+"F0.wireOp",EDGE,"E25.5"),sQuery(id+"F0.wireOp",EDGE,"E25.6"),sQuery(id+"F0.wireOp",EDGE,"E25.7")])],"isStart":false})})});
            extrude(context, id + "F13", {"entities" : qUnion([Q0]), "operationType" : NewBodyOperationType.REMOVE, "endBound" : BoundingType.UP_TO_SURFACE, "endBoundEntityFace" : qUnion([Q1]), "depth" : 25 * mm});
        }
        {
            var Q0;
            Q0=makeQuery(id+"F3.boolean.opBoolean","COPY",EDGE,{"derivedFrom":makeQuery(id+"F3.opExtrude","CAP_EDGE",EDGE,{"disambiguationData":[OSD([sQuery(id+"F0.wireOp",EDGE,"E25.6")])],"isStart":false})});
            var Q1;
            Q1=makeQuery(id+"F8.boolean.opBoolean","INTERSECT",EDGE,{"derivedFrom":[makeQuery(id+"F5.opExtrude","SWEPT_FACE",FACE,{"disambiguationData":[OSD([sQuery(id+"F4.wireOp",EDGE,"E30")])]}),makeQuery(id+"F8.opExtrude","CAP_FACE",FACE,{"disambiguationData":[OSD([sQuery(id+"F7.wireOp",EDGE,"E67")])],"isStart":false})]});
            var Q2;
            Q2=makeQuery(id+"F8.boolean.opBoolean","INTERSECT",EDGE,{"disambiguationData":[OD(1.0)],"derivedFrom":[makeQuery(id+"F5.opExtrude","SWEPT_FACE",FACE,{"disambiguationData":[OSD([sQuery(id+"F4.wireOp",EDGE,"E30")])]}),makeQuery(id+"F8.opExtrude","SWEPT_FACE",FACE,{"disambiguationData":[OSD([sQuery(id+"F7.wireOp",EDGE,"E67")])]})]});
            var Q3;
            {var subQ0=sQuery(id+"F4.wireOp",EDGE,"E30");Q3=makeQuery(id+"F8.boolean.opBoolean","SPLIT",EDGE,{"disambiguationData":[TD([makeQuery(id+"F5.opExtrude","SWEPT_FACE",FACE,{"disambiguationData":[OSD([sQuery(id+"F4.wireOp",EDGE,"E35.filletArc")])]})])],"derivedFrom":makeQuery(id+"F5.opExtrude","CAP_EDGE",EDGE,{"disambiguationData":[OSD([subQ0])],"isStart":false})});}
            var Q4;
            {var subQ0=sQuery(id+"F0.wireOp",EDGE,"E25.7");var subQ1=sQuery(id+"F0.wireOp",EDGE,"E25.1");var subQ2=sQuery(id+"F0.wireOp",EDGE,"E25.6");var subQ3=sQuery(id+"F0.wireOp",EDGE,"E25.5");var subQ4=sQuery(id+"F0.wireOp",EDGE,"E25.4");var subQ5=sQuery(id+"F0.wireOp",EDGE,"E25.0");var subQ6=sQuery(id+"F0.wireOp",EDGE,"E25.2");var subQ7=sQuery(id+"F0.wireOp",EDGE,"E25.3");Q4=makeQuery(id+"F8.boolean.opBoolean","INTERSECT",EDGE,{"derivedFrom":[makeQuery(id+"F5.boolean.opBoolean","SPLIT",FACE,{"disambiguationData":[TD([makeQuery(id+"F2.opExtrude","SWEPT_FACE",FACE,{"disambiguationData":[OSD([subQ5])]})])],"derivedFrom":makeQuery(id+"F3.boolean.opBoolean","COPY",FACE,{"derivedFrom":makeQuery(id+"F3.opExtrude","CAP_FACE",FACE,{"disambiguationData":[OSD([subQ5,subQ1,subQ6,subQ7,subQ4,subQ3,subQ2,subQ0])],"isStart":false})})}),makeQuery(id+"F8.opExtrude","SWEPT_FACE",FACE,{"disambiguationData":[OSD([sQuery(id+"F7.wireOp",EDGE,"E67")])]})]});}
            var Q5;
            Q5=makeQuery(id+"F8.boolean.opBoolean","INTERSECT",EDGE,{"disambiguationData":[OD(0.0)],"derivedFrom":[makeQuery(id+"F5.opExtrude","SWEPT_FACE",FACE,{"disambiguationData":[OSD([sQuery(id+"F4.wireOp",EDGE,"E30")])]}),makeQuery(id+"F8.opExtrude","SWEPT_FACE",FACE,{"disambiguationData":[OSD([sQuery(id+"F7.wireOp",EDGE,"E67")])]})]});
            fillet(context, id + "F14", {"entities" : qUnion([Q0, Q1, Q2, Q3, Q4, Q5]), "radius" : 3 * mm, "tangentPropagation" : true, "allowEdgeOverflow" : false});
        }
        {
            var Q0;
            Q0=makeQuery(id+"F1.opExtrude","CAP_EDGE",EDGE,{"disambiguationData":[OSD([sQuery(id+"F0.wireOp",EDGE,"E1.bottom")])],"isStart":false});
            fillet(context, id + "F15", {"entities" : qUnion([Q0]), "radius" : 2 * mm, "tangentPropagation" : true, "allowEdgeOverflow" : false});
        }
        {
            var Q0;
            {var subQ0=sQuery(id+"F0.wireOp",EDGE,"E21.filletArc");var subQ1=sQuery(id+"F0.wireOp",EDGE,"E7");var subQ2=sQuery(id+"F0.wireOp",EDGE,"E6");var subQ3=sQuery(id+"F0.wireOp",EDGE,"E5");var subQ4=sQuery(id+"F0.wireOp",EDGE,"E4");var subQ5=sQuery(id+"F0.wireOp",EDGE,"E22.filletArc");var subQ6=sQuery(id+"F0.wireOp",EDGE,"E1.bottom");var subQ7=sQuery(id+"F0.wireOp",EDGE,"E1.right");var subQ8=sQuery(id+"F0.wireOp",EDGE,"E1.top");var subQ9=sQuery(id+"F0.wireOp",EDGE,"E1.left");var subQ10=sQuery(id+"F0.wireOp",EDGE,"E23.filletArc");var subQ11=sQuery(id+"F0.wireOp",EDGE,"E24.filletArc");Q0=makeQuery(id+"F2.boolean.opBoolean","SPLIT",FACE,{"disambiguationData":[TD([makeQuery(id+"F1.opExtrude","SWEPT_FACE",FACE,{"disambiguationData":[OSD([subQ6])]})])],"derivedFrom":makeQuery(id+"F1.opExtrude","CAP_FACE",FACE,{"disambiguationData":[OSD([subQ6,subQ8,subQ9,subQ7,subQ4,subQ3,subQ2,subQ1,subQ0,subQ5,subQ10,subQ11])],"isStart":true})});}
            var sketch = newSketch(context, id + "F16", { "sketchPlane" : qUnion([Q0])});
            skLineSegment(sketch, "E79", {"start": v(0, 74.25) * mm, "end": v(0, 104.25) * mm, "construction": true});
            skArc(sketch, "E80", {"start": v(15, 104.25) * mm, "mid": v(0, 119.25) * mm, "end": v(-15, 104.25) * mm});
            skCircle(sketch, "E81", {"center": v(0, 104.25) * mm, "radius": 6 * mm});
            skLineSegment(sketch, "E82", {"start": v(-15, 104.25) * mm, "end": v(-15, 95.12) * mm});
            skLineSegment(sketch, "E83", {"start": v(15, 104.25) * mm, "end": v(15, 94.96) * mm});
            skLineSegment(sketch, "E84", {"start": v(-15, 95.12) * mm, "end": v(-35.87, 74.25) * mm});
            skLineSegment(sketch, "E85", {"start": v(15, 94.96) * mm, "end": v(35.71, 74.25) * mm});
            skLineSegment(sketch, "E86", {"start": v(-74.25, 0) * mm, "end": v(74.25, 0) * mm});
            skLineSegment(sketch, "E87.MirrorCS", {"start": v(15, -94.96) * mm, "end": v(35.71, -74.25) * mm});
            skLineSegment(sketch, "E88.MirrorCS", {"start": v(0, -74.25) * mm, "end": v(0, -104.25) * mm, "construction": true});
            skLineSegment(sketch, "E89.MirrorCS", {"start": v(-15, -95.12) * mm, "end": v(-35.87, -74.25) * mm});
            skLineSegment(sketch, "E90.MirrorCS", {"start": v(-15, -104.25) * mm, "end": v(-15, -95.12) * mm});
            skArc(sketch, "E91.MirrorCS", {"start": v(15, -104.25) * mm, "mid": v(0, -119.25) * mm, "end": v(-15, -104.25) * mm});
            skLineSegment(sketch, "E92.MirrorCS", {"start": v(15, -104.25) * mm, "end": v(15, -94.96) * mm});
            skCircle(sketch, "E93.MirrorC", {"center": v(0, -104.25) * mm, "radius": 6 * mm});
            skSolve(sketch);
        }
        {
            var Q0;
            Q0=makeQuery(id+"F16.imprint","IMPRINT",FACE,{"disambiguationData":[TD([[makeQuery(id+"F16.imprint","IMPRINT",EDGE,{"derivedFrom":makeQuery(id+"F1.opExtrude","CAP_EDGE",EDGE,{"disambiguationData":[OSD([sQuery(id+"F0.wireOp",EDGE,"E4")])],"isStart":true})}),-1.0]])]});
            var Q1;
            Q1=makeQuery(id+"F16.imprint","IMPRINT",FACE,{"disambiguationData":[TD([[makeQuery(id+"F16.imprint","IMPRINT",EDGE,{"derivedFrom":makeQuery(id+"F1.opExtrude","CAP_EDGE",EDGE,{"disambiguationData":[OSD([sQuery(id+"F0.wireOp",EDGE,"E6")])],"isStart":true})}),-1.0]])]});
            var Q2;
            Q2=makeQuery(id+"F16.imprint","IMPRINT",FACE,{"disambiguationData":[TD([[makeQuery(id+"F16.imprint","IMPRINT",EDGE,{"derivedFrom":sQuery(id+"F16.wireOp",EDGE,"E80")}),1.0]])]});
            var Q3;
            {var subQ1=sQuery(id+"F16.wireOp",EDGE,"E87.MirrorCS");Q3=makeQuery(id+"F16.imprint","IMPRINT",FACE,{"disambiguationData":[TD([[makeQuery(id+"F16.imprint","IMPRINT",EDGE,{"derivedFrom":subQ1}),1.0]])]});}
            extrude(context, id + "F17", {"entities" : qUnion([Q0, Q1, Q2, Q3]), "depth" : 5 * mm});
        }
    });
